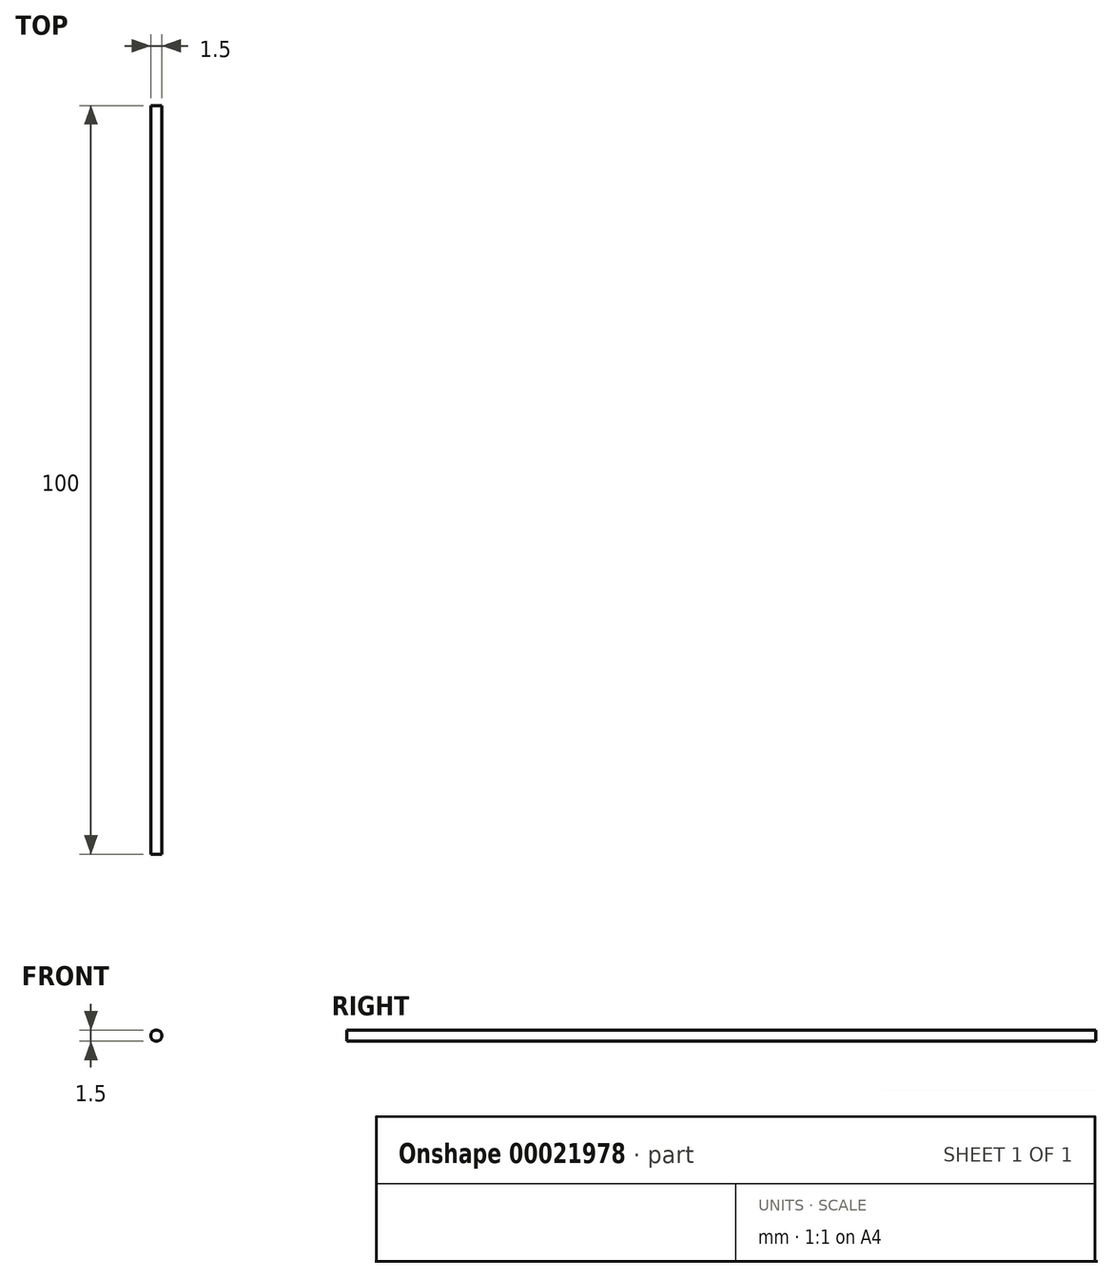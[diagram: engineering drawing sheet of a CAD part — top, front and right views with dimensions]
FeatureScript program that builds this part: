
annotation { "Feature Type Name" : "Feature", "Feature Type Description" : "" }
export const myFeature = defineFeature(function(context is Context, id is Id, definition is map)
    precondition{}
    {
        {
            var Q0;
            Q0=qCreatedBy(makeId("Front.planeOp"),FACE);
            var sketch = newSketch(context, id + "F0", { "sketchPlane" : qUnion([Q0])});
            skCircle(sketch, "E0", {"center": v(0, 0) * mm, "radius": 0.75 * mm});
            skSolve(sketch);
        }
        {
            var Q0;
            Q0 = qSketchRegion(id + "F0", true);
            extrude(context, id + "F1", {"entities" : qUnion([Q0]), "depth" : 100 * mm});
        }
    });
